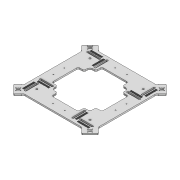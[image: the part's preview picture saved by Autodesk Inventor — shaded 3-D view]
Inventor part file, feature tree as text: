
AUTODESK INVENTOR PART (.ipt)
format: ipt  version: 2020 (Build 240168000, 168)  size: 1,200,640 bytes
history: native  units: mm
features: sketch x3, extrude x2, fillet x2, chamfer x1, mirror x1
ambient origin geometry x8: Origin, YZ Plane, XZ Plane, XY Plane, X Axis, Y Axis, Z Axis, Center Point
bodies: Solid1 (feature_tree)
feature tree (9):
  extrude  "Extrusion1"  Depth=3.0mm
  extrude  "Extrusion2"  Depth=10.0mm TaperAngle=0.0deg
  sketch  "Sketch4"  dims[d7=3.0mm d8=18.5mm d9=20.0mm d10=10.0mm d11=0.0mm d12=6.0mm d13=2.0mm d14=45.0deg d15=3.0mm d16=7.0mm]
  chamfer  "Chamfer1"  Distance=18.5mm
  fillet  "Fillet1"  Radius=20.0mm
  fillet  "Fillet2"  Radius=10.0mm
  sketch  "Sketch2"  dims[d2=20.0mm d3=3.0mm]
  sketch  "Sketch3"  dims[d4=20.0mm d5=10.0mm d6=0.0mm]
  mirror  "Mirror7"
